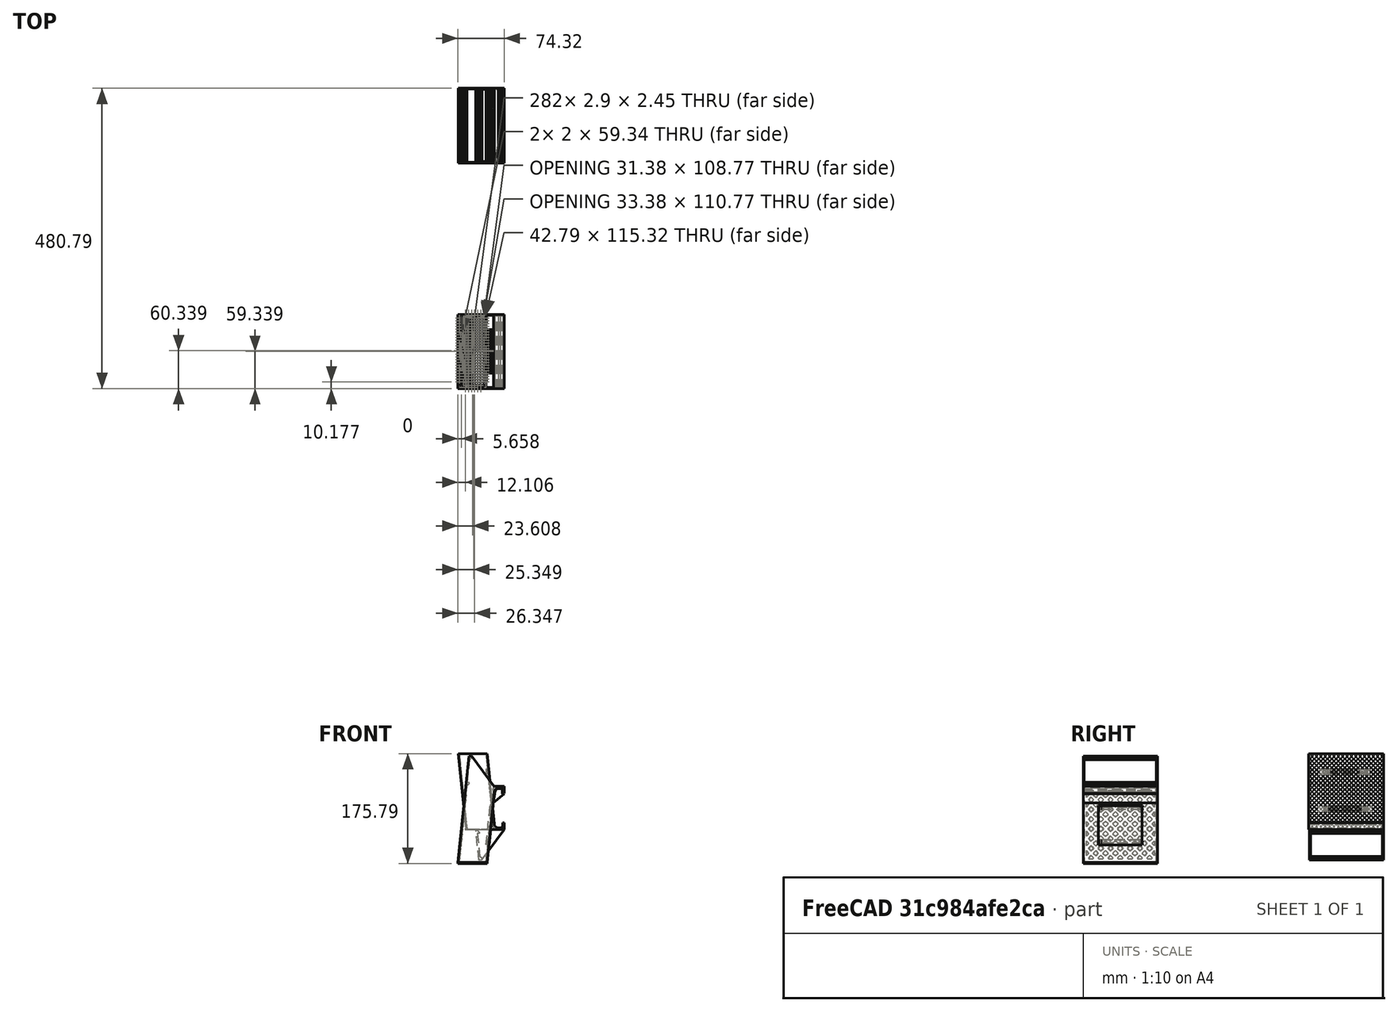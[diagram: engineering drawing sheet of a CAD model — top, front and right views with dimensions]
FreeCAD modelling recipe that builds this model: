
FCSTD DOCUMENT  (FreeCAD 0.18.4R)
Label: tmp
License: All rights reserved
LicenseURL: http://en.wikipedia.org/wiki/All_rights_reserved
objects: Part::FeaturePython×7, Part::Feature×4, Part::Part2DObjectPython×4, App::DocumentObjectGroup×3, Part::MultiFuse×1, Part::Extrusion×1
note: 17 computed .brp shape members not serialized (recipe doc carries the construction recipe); baked Part::Feature solids carry a one-line shape summary decoded from their .brp

FEATURE [Part::Feature] Fusion002003010002002002002002003010002002005001  label="Fusion002003010002002002002002003010002002006"
  shape: bbox 74.18 x 118.7 x 172 mm, 1267 faces (baked)
FEATURE [Part::MultiFuse] Fusion002003010002002002002002003010002003
FEATURE [Part::Part2DObjectPython] Rectangle  # Draft 2D object (typed FeaturePython)
  ChamferSize = 0
  Columns = 1
  FilletRadius = 0
  Height = 70.3308
  Length = 63.2635
  MakeFace = true
  Placement = pos=(142.156,-379.085,-156.131) rot=(0.741992,0,0.670408;3.14159rad)
  Rows = 1
FEATURE [Part::Extrusion] Extrusion
  Base = -> Rectangle
  Dir = (-4.5175,2.81e-14,0.459096)
  DirMode = 0
  FaceMakerClass = Part::FaceMakerBullseye
  LengthFwd = 0
  LengthRev = 0
  Solid = true
  Symmetric = false
FEATURE [Part::Part2DObjectPython] Rectangle001  # Draft 2D object (typed FeaturePython)
  ChamferSize = 0
  Columns = 1
  FilletRadius = 0
  Height = 241
  Length = 62
  MakeFace = true
  Placement = pos=(135.021,-259.207,-226.326) rot=(0.741992,0,0.670408;3.14159rad)
  Rows = 1
  Support = -> [Fusion002003010002002002002002003010002002005001]
FEATURE [Part::FeaturePython] Slice  # WARN: FeaturePython — macro-defined, semantics opaque (R4)
  Base = -> Fusion002003010002002002002002003010002002005001
  Mode = 1
  Tolerance = 0
  Tools = -> [Rectangle001]
FEATURE [Part::FeaturePython] Slice_child0  label="Slice.0"  # WARN: FeaturePython — macro-defined, semantics opaque (R4)
  Base = -> Slice
  FilterType = 1
  Invert = false
  OverrideMaxVal = 0
  WindowFrom = 80
  WindowTo = 100
  items = 0
FEATURE [App::DocumentObjectGroup] GrExplode_Slice  label="Exploded Slice"
  Group = -> [Slice_child0]
FEATURE [Part::Feature] Slice_child0001  label="Slice.001"
  shape: bbox 74.18 x 118.7 x 172 mm, 1266 faces (baked)
FEATURE [Part::Part2DObjectPython] Rectangle003  # Draft 2D object (typed FeaturePython)
  ChamferSize = 0
  Columns = 1
  FilletRadius = 0
  Height = 276
  Length = 161
  MakeFace = true
  Placement = pos=(29.0751,-560.327,-183.654) rot=(0,0,1;0rad)
  Rows = 1
  Support = -> [Slice_child0001]
FEATURE [Part::FeaturePython] Slice001  # WARN: FeaturePython — macro-defined, semantics opaque (R4)
  Base = -> Slice_child0001
  Mode = 1
  Tolerance = 0
  Tools = -> [Rectangle003]
FEATURE [Part::FeaturePython] Slice001_child0  label="Slice001.0"  # WARN: FeaturePython — macro-defined, semantics opaque (R4)
  Base = -> Slice001
  FilterType = 1
  Invert = false
  OverrideMaxVal = 0
  WindowFrom = 80
  WindowTo = 100
  items = 0
FEATURE [Part::FeaturePython] Slice001_child1  label="Slice001.1"  # WARN: FeaturePython — macro-defined, semantics opaque (R4)
  Base = -> Slice001
  FilterType = 1
  Invert = false
  OverrideMaxVal = 0
  WindowFrom = 80
  WindowTo = 100
  items = 1
FEATURE [App::DocumentObjectGroup] GrExplode_Slice001  label="Exploded Slice001"
  Group = -> [Slice001_child0,Slice001_child1]
FEATURE [Part::Feature] Fusion002003010002002002002002003010002002005002  label="Fusion002003010002002002002002003010002002007"
  shape: bbox 74.18 x 118.7 x 172 mm, 1267 faces (baked)
FEATURE [Part::Feature] Fusion018002001008016001  label="Fusion018002001008017"
  shape: bbox 73.48 x 120 x 121.6 mm, 4427 faces (baked)
FEATURE [Part::Part2DObjectPython] Rectangle004  # Draft 2D object (typed FeaturePython)
  ChamferSize = 0
  Columns = 1
  FilletRadius = 0
  Height = 199
  Length = 146
  MakeFace = true
  Placement = pos=(74.114,-529.231,-62.252) rot=(0,0,1;0rad)
  Rows = 1
  Support = -> [Fusion002003010002002002002002003010002002005002]
FEATURE [Part::FeaturePython] Slice002  # WARN: FeaturePython — macro-defined, semantics opaque (R4)
  Base = -> Fusion002003010002002002002002003010002002005002
  Mode = 1
  Tolerance = 0
  Tools = -> [Rectangle004]
FEATURE [Part::FeaturePython] Slice_child0002  label="Slice.002"  # WARN: FeaturePython — macro-defined, semantics opaque (R4)
  Base = -> Slice002
  FilterType = 1
  Invert = false
  OverrideMaxVal = 0
  Placement = pos=(16.1242,-466.35,-193.634) rot=(1,0,0;3.14159rad)
  WindowFrom = 80
  WindowTo = 100
  items = 0
FEATURE [App::DocumentObjectGroup] GrExplode_Slice002  label="Exploded Slice002"
  Group = -> [Slice_child0002]
